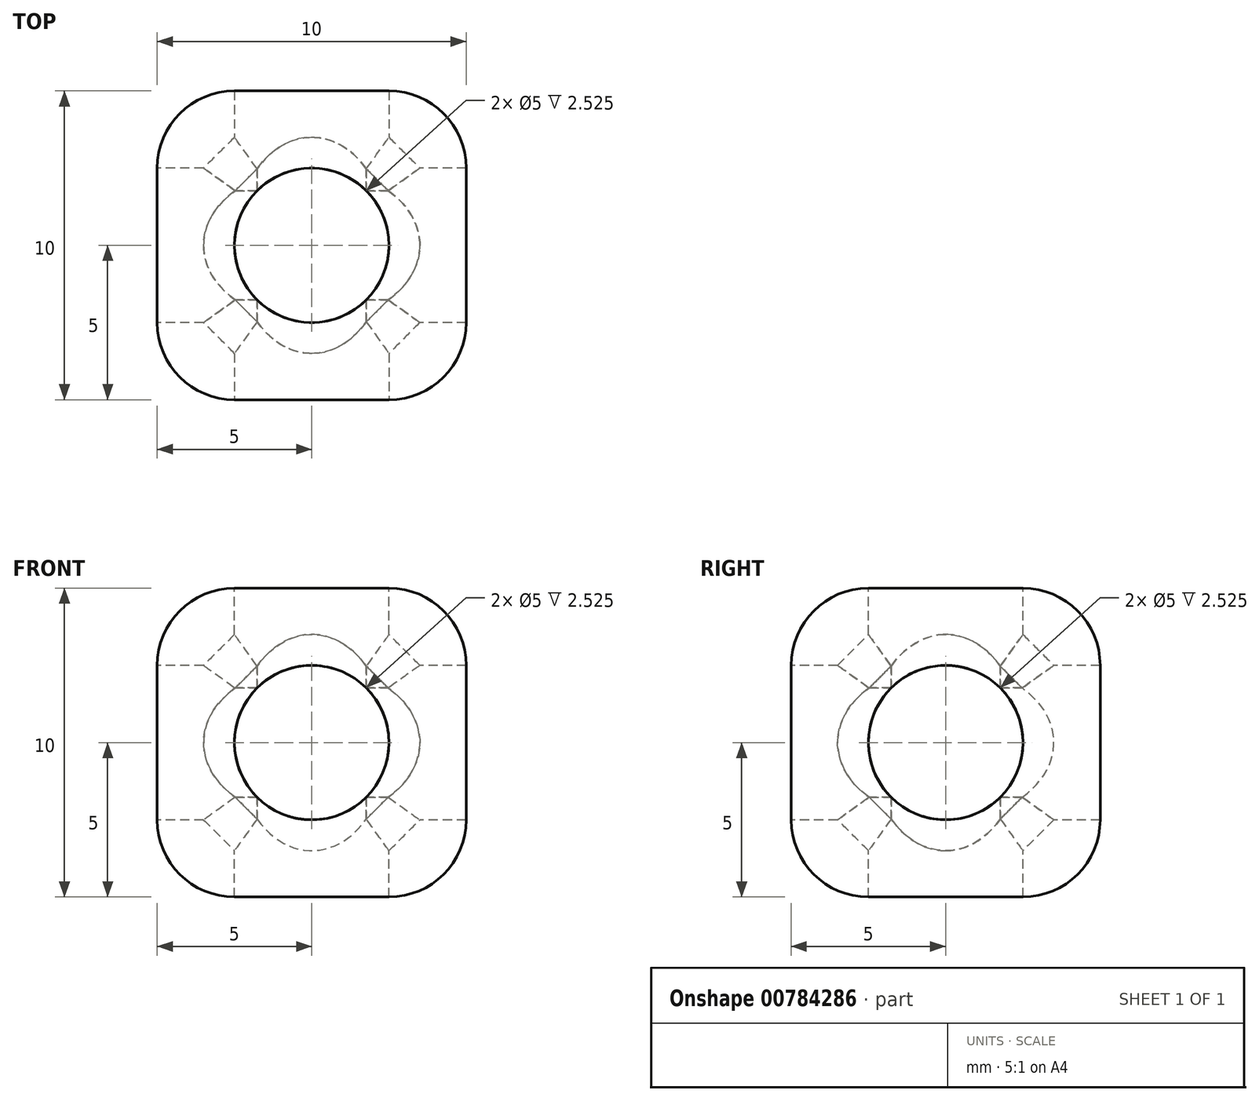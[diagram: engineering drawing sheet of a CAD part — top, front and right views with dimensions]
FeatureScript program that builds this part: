
annotation { "Feature Type Name" : "Feature", "Feature Type Description" : "" }
export const myFeature = defineFeature(function(context is Context, id is Id, definition is map)
    precondition{}
    {
        {
            var Q0;
            Q0=qCreatedBy(makeId("Front.planeOp"),FACE);
            var sketch = newSketch(context, id + "F0", { "sketchPlane" : qUnion([Q0])});
            skLineSegment(sketch, "E0.bottom", {"start": v(5, 5) * mm, "end": v(-5, 5) * mm});
            skLineSegment(sketch, "E0.top", {"start": v(5, -5) * mm, "end": v(-5, -5) * mm});
            skLineSegment(sketch, "E0.left", {"start": v(5, 5) * mm, "end": v(5, -5) * mm});
            skLineSegment(sketch, "E0.right", {"start": v(-5, 5) * mm, "end": v(-5, -5) * mm});
            skPoint(sketch, "E0.middle", {"position": v(0, 0) * mm});
            skSolve(sketch);
        }
        {
            var Q0;
            Q0=makeQuery(id+"F0.imprint","IMPRINT",FACE,{"disambiguationData":[TD([[makeQuery(id+"F0.imprint","IMPRINT",EDGE,{"derivedFrom":sQuery(id+"F0.wireOp",EDGE,"E0.bottom")}),1.0]])]});
            extrude(context, id + "F1", {"entities" : qUnion([Q0]), "endBound" : BoundingType.SYMMETRIC, "depth" : 10 * mm, "offsetDistance" : 25 * mm});
        }
        {
            var Q0;
            Q0=makeQuery(id+"F1.opExtrude","SWEPT_EDGE",EDGE,{"disambiguationData":[OSD([sQuery(id+"F0.wireOp",EDGE,"E0.bottom"),sQuery(id+"F0.wireOp",EDGE,"E0.right")])]});
            var Q1;
            Q1=makeQuery(id+"F1.opExtrude","CAP_EDGE",EDGE,{"disambiguationData":[OSD([sQuery(id+"F0.wireOp",EDGE,"E0.bottom")])],"isStart":false});
            var Q2;
            Q2=makeQuery(id+"F1.opExtrude","SWEPT_EDGE",EDGE,{"disambiguationData":[OSD([sQuery(id+"F0.wireOp",EDGE,"E0.bottom"),sQuery(id+"F0.wireOp",EDGE,"E0.left")])]});
            var Q3;
            Q3=makeQuery(id+"F1.opExtrude","CAP_EDGE",EDGE,{"disambiguationData":[OSD([sQuery(id+"F0.wireOp",EDGE,"E0.bottom")])],"isStart":true});
            var Q4;
            Q4=makeQuery(id+"F1.opExtrude","CAP_EDGE",EDGE,{"disambiguationData":[OSD([sQuery(id+"F0.wireOp",EDGE,"E0.right")])],"isStart":false});
            var Q5;
            Q5=makeQuery(id+"F1.opExtrude","CAP_EDGE",EDGE,{"disambiguationData":[OSD([sQuery(id+"F0.wireOp",EDGE,"E0.left")])],"isStart":false});
            var Q6;
            Q6=makeQuery(id+"F1.opExtrude","CAP_EDGE",EDGE,{"disambiguationData":[OSD([sQuery(id+"F0.wireOp",EDGE,"E0.left")])],"isStart":true});
            var Q7;
            Q7=makeQuery(id+"F1.opExtrude","CAP_EDGE",EDGE,{"disambiguationData":[OSD([sQuery(id+"F0.wireOp",EDGE,"E0.right")])],"isStart":true});
            var Q8;
            Q8=makeQuery(id+"F1.opExtrude","SWEPT_FACE",FACE,{"disambiguationData":[OSD([sQuery(id+"F0.wireOp",EDGE,"E0.top")])]});
            fillet(context, id + "F2", {"entities" : qUnion([Q0, Q1, Q2, Q3, Q4, Q5, Q6, Q7, Q8]), "radius" : 2.5 * mm, "tangentPropagation" : true, "allowEdgeOverflow" : false});
        }
        {
            var Q0;
            Q0=makeQuery(id+"F1.opExtrude","SWEPT_FACE",FACE,{"disambiguationData":[OSD([sQuery(id+"F0.wireOp",EDGE,"E0.right")])]});
            var sketch = newSketch(context, id + "F3", { "sketchPlane" : qUnion([Q0])});
            skCircle(sketch, "E1", {"center": v(0, 0) * mm, "radius": 2.5 * mm});
            skSolve(sketch);
        }
        {
            var Q0;
            Q0=makeQuery(id+"F1.opExtrude","CAP_FACE",FACE,{"disambiguationData":[OSD([sQuery(id+"F0.wireOp",EDGE,"E0.bottom"),sQuery(id+"F0.wireOp",EDGE,"E0.top"),sQuery(id+"F0.wireOp",EDGE,"E0.left"),sQuery(id+"F0.wireOp",EDGE,"E0.right")])],"isStart":false});
            var sketch = newSketch(context, id + "F4", { "sketchPlane" : qUnion([Q0])});
            skCircle(sketch, "E2", {"center": v(0, 0) * mm, "radius": 2.5 * mm});
            skSolve(sketch);
        }
        {
            var Q0;
            Q0=makeQuery(id+"F1.opExtrude","SWEPT_FACE",FACE,{"disambiguationData":[OSD([sQuery(id+"F0.wireOp",EDGE,"E0.bottom")])]});
            var sketch = newSketch(context, id + "F5", { "sketchPlane" : qUnion([Q0])});
            skCircle(sketch, "E3", {"center": v(0, 0) * mm, "radius": 2.5 * mm});
            skSolve(sketch);
        }
        {
            var Q0;
            {var subQ0=sQuery(id+"F5.wireOp",EDGE,"E3");var subQ1=sQuery(id+"F0.wireOp",EDGE,"E0.bottom");var subQ2=makeQuery(id+"F1.opExtrude","SWEPT_FACE",FACE,{"disambiguationData":[OSD([subQ1])]});var subQ3=makeQuery(id+"F5.imprint","INTERSECT",VERTEX,{"derivedFrom":[makeQuery(id+"F2.opFillet","BLEND_EDGE",EDGE,{"blendedFrom":[makeQuery(id+"F1.opExtrude","CAP_EDGE",EDGE,{"disambiguationData":[OSD([subQ1])],"isStart":true}),subQ2],"blendedInto":[subQ2]}),subQ0]});Q0=makeQuery(id+"F5.imprint","IMPRINT",FACE,{"disambiguationData":[TD([[makeQuery(id+"F5.imprint","IMPRINT",EDGE,{"disambiguationData":[TD([[subQ3,1.0]])],"derivedFrom":subQ0}),1.0]])]});}
            extrude(context, id + "F6", {"entities" : qUnion([Q0]), "operationType" : NewBodyOperationType.REMOVE, "oppositeDirection" : true, "depth" : 25 * mm, "offsetDistance" : 25 * mm});
        }
        {
            var Q0;
            {var subQ0=sQuery(id+"F3.wireOp",EDGE,"E1");var subQ1=sQuery(id+"F0.wireOp",EDGE,"E0.right");var subQ2=makeQuery(id+"F1.opExtrude","SWEPT_FACE",FACE,{"disambiguationData":[OSD([subQ1])]});var subQ4=makeQuery(id+"F3.imprint","INTERSECT",VERTEX,{"derivedFrom":[makeQuery(id+"F2.opFillet","BLEND_EDGE",EDGE,{"blendedFrom":[makeQuery(id+"F1.opExtrude","CAP_EDGE",EDGE,{"disambiguationData":[OSD([subQ1])],"isStart":false}),subQ2],"blendedInto":[subQ2]}),subQ0]});Q0=makeQuery(id+"F3.imprint","IMPRINT",FACE,{"disambiguationData":[TD([[makeQuery(id+"F3.imprint","IMPRINT",EDGE,{"disambiguationData":[TD([[subQ4,-1.0]])],"derivedFrom":subQ0}),1.0]])]});}
            extrude(context, id + "F7", {"entities" : qUnion([Q0]), "operationType" : NewBodyOperationType.REMOVE, "oppositeDirection" : true, "depth" : 25 * mm, "offsetDistance" : 25 * mm});
        }
        {
            var Q0;
            {var subQ0=sQuery(id+"F4.wireOp",EDGE,"E2");var subQ1=sQuery(id+"F0.wireOp",EDGE,"E0.right");var subQ2=sQuery(id+"F0.wireOp",EDGE,"E0.left");var subQ3=sQuery(id+"F0.wireOp",EDGE,"E0.top");var subQ4=sQuery(id+"F0.wireOp",EDGE,"E0.bottom");var subQ5=makeQuery(id+"F1.opExtrude","CAP_FACE",FACE,{"disambiguationData":[OSD([subQ4,subQ3,subQ2,subQ1])],"isStart":false});var subQ6=makeQuery(id+"F4.imprint","INTERSECT",VERTEX,{"derivedFrom":[makeQuery(id+"F2.opFillet","BLEND_EDGE",EDGE,{"blendedFrom":[makeQuery(id+"F1.opExtrude","CAP_EDGE",EDGE,{"disambiguationData":[OSD([subQ4])],"isStart":false}),subQ5],"blendedInto":[subQ5]}),subQ0]});Q0=makeQuery(id+"F4.imprint","IMPRINT",FACE,{"disambiguationData":[TD([[makeQuery(id+"F4.imprint","IMPRINT",EDGE,{"disambiguationData":[TD([[subQ6,1.0]])],"derivedFrom":subQ0}),1.0]])]});}
            extrude(context, id + "F8", {"entities" : qUnion([Q0]), "operationType" : NewBodyOperationType.REMOVE, "oppositeDirection" : true, "depth" : 25 * mm, "offsetDistance" : 25 * mm});
        }
        {
            var Q0;
            Q0=makeQuery(id+"F7.boolean.opBoolean","INTERSECT",EDGE,{"disambiguationData":[OD(0.0)],"derivedFrom":[makeQuery(id+"F6.boolean.opBoolean","COPY",FACE,{"derivedFrom":makeQuery(id+"F6.opExtrude","SWEPT_FACE",FACE,{"disambiguationData":[OSD([sQuery(id+"F5.wireOp",EDGE,"E3")])]})}),makeQuery(id+"F7.opExtrude","SWEPT_FACE",FACE,{"disambiguationData":[OSD([sQuery(id+"F3.wireOp",EDGE,"E1")])]})]});
            var Q1;
            {var subQ0=sQuery(id+"F0.wireOp",EDGE,"E0.top");var subQ3=makeQuery(id+"F6.boolean.opBoolean","COPY",FACE,{"derivedFrom":makeQuery(id+"F6.opExtrude","SWEPT_FACE",FACE,{"disambiguationData":[OSD([sQuery(id+"F5.wireOp",EDGE,"E3")])]})});Q1=makeQuery(id+"F8.boolean.opBoolean","INTERSECT",EDGE,{"disambiguationData":[OD(1.0)],"derivedFrom":[makeQuery(id+"F7.boolean.opBoolean","SPLIT",FACE,{"disambiguationData":[TD([makeQuery(id+"F1.opExtrude","SWEPT_FACE",FACE,{"disambiguationData":[OSD([subQ0])]})])],"derivedFrom":subQ3}),makeQuery(id+"F8.opExtrude","SWEPT_FACE",FACE,{"disambiguationData":[OSD([sQuery(id+"F4.wireOp",EDGE,"E2")])]})]});}
            var Q2;
            {var subQ0=sQuery(id+"F0.wireOp",EDGE,"E0.left");var subQ3=makeQuery(id+"F7.opExtrude","SWEPT_FACE",FACE,{"disambiguationData":[OSD([sQuery(id+"F3.wireOp",EDGE,"E1")])]});Q2=makeQuery(id+"F8.boolean.opBoolean","INTERSECT",EDGE,{"disambiguationData":[OD(1.0)],"derivedFrom":[makeQuery(id+"F7.boolean.opBoolean","COPY",FACE,{"disambiguationData":[TD([makeQuery(id+"F1.opExtrude","SWEPT_FACE",FACE,{"disambiguationData":[OSD([subQ0])]})])],"derivedFrom":subQ3}),makeQuery(id+"F8.opExtrude","SWEPT_FACE",FACE,{"disambiguationData":[OSD([sQuery(id+"F4.wireOp",EDGE,"E2")])]})]});}
            var Q3;
            Q3=makeQuery(id+"F7.boolean.opBoolean","INTERSECT",EDGE,{"disambiguationData":[OD(2.0)],"derivedFrom":[makeQuery(id+"F6.boolean.opBoolean","COPY",FACE,{"derivedFrom":makeQuery(id+"F6.opExtrude","SWEPT_FACE",FACE,{"disambiguationData":[OSD([sQuery(id+"F5.wireOp",EDGE,"E3")])]})}),makeQuery(id+"F7.opExtrude","SWEPT_FACE",FACE,{"disambiguationData":[OSD([sQuery(id+"F3.wireOp",EDGE,"E1")])]})]});
            var Q4;
            {var subQ0=sQuery(id+"F0.wireOp",EDGE,"E0.bottom");var subQ3=makeQuery(id+"F6.boolean.opBoolean","COPY",FACE,{"derivedFrom":makeQuery(id+"F6.opExtrude","SWEPT_FACE",FACE,{"disambiguationData":[OSD([sQuery(id+"F5.wireOp",EDGE,"E3")])]})});Q4=makeQuery(id+"F8.boolean.opBoolean","INTERSECT",EDGE,{"disambiguationData":[OD(1.0)],"derivedFrom":[makeQuery(id+"F7.boolean.opBoolean","SPLIT",FACE,{"disambiguationData":[TD([makeQuery(id+"F1.opExtrude","SWEPT_FACE",FACE,{"disambiguationData":[OSD([subQ0])]})])],"derivedFrom":subQ3}),makeQuery(id+"F8.opExtrude","SWEPT_FACE",FACE,{"disambiguationData":[OSD([sQuery(id+"F4.wireOp",EDGE,"E2")])]})]});}
            var Q5;
            {var subQ0=sQuery(id+"F0.wireOp",EDGE,"E0.right");var subQ3=makeQuery(id+"F7.opExtrude","SWEPT_FACE",FACE,{"disambiguationData":[OSD([sQuery(id+"F3.wireOp",EDGE,"E1")])]});Q5=makeQuery(id+"F8.boolean.opBoolean","INTERSECT",EDGE,{"disambiguationData":[OD(1.0)],"derivedFrom":[makeQuery(id+"F7.boolean.opBoolean","COPY",FACE,{"disambiguationData":[TD([makeQuery(id+"F1.opExtrude","SWEPT_FACE",FACE,{"disambiguationData":[OSD([subQ0])]})])],"derivedFrom":subQ3}),makeQuery(id+"F8.opExtrude","SWEPT_FACE",FACE,{"disambiguationData":[OSD([sQuery(id+"F4.wireOp",EDGE,"E2")])]})]});}
            var Q6;
            Q6=makeQuery(id+"F7.boolean.opBoolean","INTERSECT",EDGE,{"disambiguationData":[OD(3.0)],"derivedFrom":[makeQuery(id+"F6.boolean.opBoolean","COPY",FACE,{"derivedFrom":makeQuery(id+"F6.opExtrude","SWEPT_FACE",FACE,{"disambiguationData":[OSD([sQuery(id+"F5.wireOp",EDGE,"E3")])]})}),makeQuery(id+"F7.opExtrude","SWEPT_FACE",FACE,{"disambiguationData":[OSD([sQuery(id+"F3.wireOp",EDGE,"E1")])]})]});
            var Q7;
            Q7=makeQuery(id+"F7.boolean.opBoolean","INTERSECT",EDGE,{"disambiguationData":[OD(1.0)],"derivedFrom":[makeQuery(id+"F6.boolean.opBoolean","COPY",FACE,{"derivedFrom":makeQuery(id+"F6.opExtrude","SWEPT_FACE",FACE,{"disambiguationData":[OSD([sQuery(id+"F5.wireOp",EDGE,"E3")])]})}),makeQuery(id+"F7.opExtrude","SWEPT_FACE",FACE,{"disambiguationData":[OSD([sQuery(id+"F3.wireOp",EDGE,"E1")])]})]});
            var Q8;
            {var subQ0=sQuery(id+"F0.wireOp",EDGE,"E0.bottom");var subQ3=makeQuery(id+"F6.boolean.opBoolean","COPY",FACE,{"derivedFrom":makeQuery(id+"F6.opExtrude","SWEPT_FACE",FACE,{"disambiguationData":[OSD([sQuery(id+"F5.wireOp",EDGE,"E3")])]})});Q8=makeQuery(id+"F8.boolean.opBoolean","INTERSECT",EDGE,{"disambiguationData":[OD(0.0)],"derivedFrom":[makeQuery(id+"F7.boolean.opBoolean","SPLIT",FACE,{"disambiguationData":[TD([makeQuery(id+"F1.opExtrude","SWEPT_FACE",FACE,{"disambiguationData":[OSD([subQ0])]})])],"derivedFrom":subQ3}),makeQuery(id+"F8.opExtrude","SWEPT_FACE",FACE,{"disambiguationData":[OSD([sQuery(id+"F4.wireOp",EDGE,"E2")])]})]});}
            var Q9;
            {var subQ0=sQuery(id+"F0.wireOp",EDGE,"E0.right");var subQ3=makeQuery(id+"F7.opExtrude","SWEPT_FACE",FACE,{"disambiguationData":[OSD([sQuery(id+"F3.wireOp",EDGE,"E1")])]});Q9=makeQuery(id+"F8.boolean.opBoolean","INTERSECT",EDGE,{"disambiguationData":[OD(0.0)],"derivedFrom":[makeQuery(id+"F7.boolean.opBoolean","COPY",FACE,{"disambiguationData":[TD([makeQuery(id+"F1.opExtrude","SWEPT_FACE",FACE,{"disambiguationData":[OSD([subQ0])]})])],"derivedFrom":subQ3}),makeQuery(id+"F8.opExtrude","SWEPT_FACE",FACE,{"disambiguationData":[OSD([sQuery(id+"F4.wireOp",EDGE,"E2")])]})]});}
            var Q10;
            {var subQ0=sQuery(id+"F0.wireOp",EDGE,"E0.top");var subQ3=makeQuery(id+"F6.boolean.opBoolean","COPY",FACE,{"derivedFrom":makeQuery(id+"F6.opExtrude","SWEPT_FACE",FACE,{"disambiguationData":[OSD([sQuery(id+"F5.wireOp",EDGE,"E3")])]})});Q10=makeQuery(id+"F8.boolean.opBoolean","INTERSECT",EDGE,{"disambiguationData":[OD(0.0)],"derivedFrom":[makeQuery(id+"F7.boolean.opBoolean","SPLIT",FACE,{"disambiguationData":[TD([makeQuery(id+"F1.opExtrude","SWEPT_FACE",FACE,{"disambiguationData":[OSD([subQ0])]})])],"derivedFrom":subQ3}),makeQuery(id+"F8.opExtrude","SWEPT_FACE",FACE,{"disambiguationData":[OSD([sQuery(id+"F4.wireOp",EDGE,"E2")])]})]});}
            var Q11;
            {var subQ0=sQuery(id+"F0.wireOp",EDGE,"E0.left");var subQ3=makeQuery(id+"F7.opExtrude","SWEPT_FACE",FACE,{"disambiguationData":[OSD([sQuery(id+"F3.wireOp",EDGE,"E1")])]});Q11=makeQuery(id+"F8.boolean.opBoolean","INTERSECT",EDGE,{"disambiguationData":[OD(0.0)],"derivedFrom":[makeQuery(id+"F7.boolean.opBoolean","COPY",FACE,{"disambiguationData":[TD([makeQuery(id+"F1.opExtrude","SWEPT_FACE",FACE,{"disambiguationData":[OSD([subQ0])]})])],"derivedFrom":subQ3}),makeQuery(id+"F8.opExtrude","SWEPT_FACE",FACE,{"disambiguationData":[OSD([sQuery(id+"F4.wireOp",EDGE,"E2")])]})]});}
            chamfer(context, id + "F9", {"entities" : qUnion([Q0, Q1, Q2, Q3, Q4, Q5, Q6, Q7, Q8, Q9, Q10, Q11]), "width" : 1 * mm, "tangentPropagation" : true});
        }
    });
